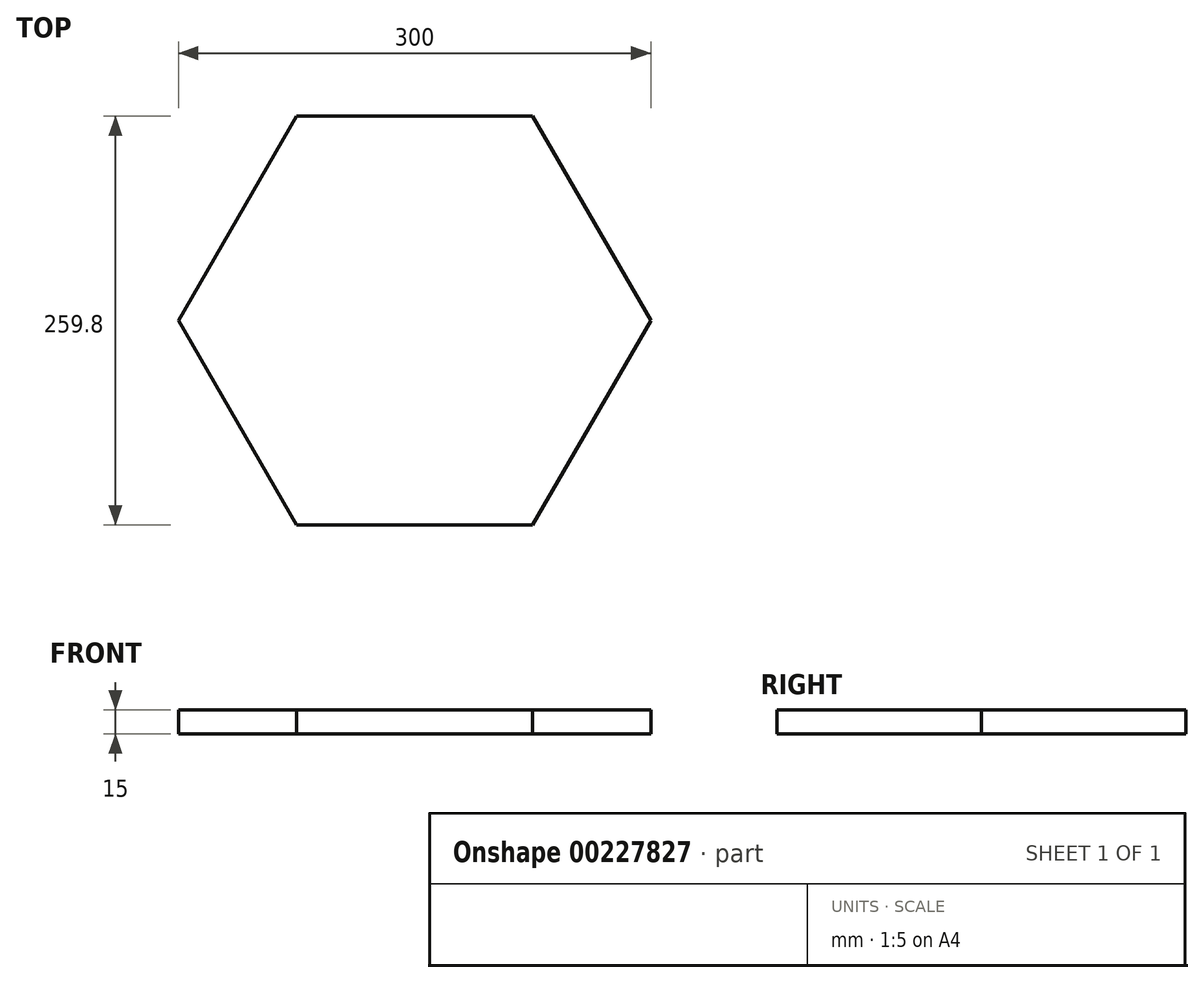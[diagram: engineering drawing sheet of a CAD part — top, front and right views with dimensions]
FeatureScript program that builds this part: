
annotation { "Feature Type Name" : "Feature", "Feature Type Description" : "" }
export const myFeature = defineFeature(function(context is Context, id is Id, definition is map)
    precondition{}
    {
        {
            var Q0;
            Q0=qCreatedBy(makeId("Top.planeOp"),FACE);
            var sketch = newSketch(context, id + "F0", { "sketchPlane" : qUnion([Q0])});
            skCircle(sketch, "E0.cCircle", {"center": v(0, 0) * mm, "radius": 150 * mm, "construction": true});
            skLineSegment(sketch, "E0.0", {"start": v(-150, 0) * mm, "end": v(-75, 129.9) * mm});
            skLineSegment(sketch, "E0.1", {"start": v(-75, 129.9) * mm, "end": v(75, 129.9) * mm});
            skLineSegment(sketch, "E0.2", {"start": v(75, 129.9) * mm, "end": v(150, 0) * mm});
            skLineSegment(sketch, "E0.3", {"start": v(150, 0) * mm, "end": v(75, -129.9) * mm});
            skLineSegment(sketch, "E0.4", {"start": v(75, -129.9) * mm, "end": v(-75, -129.9) * mm});
            skLineSegment(sketch, "E0.5", {"start": v(-75, -129.9) * mm, "end": v(-150, 0) * mm});
            skSolve(sketch);
        }
        {
            var Q0;
            Q0=makeQuery(id+"F0.imprint","IMPRINT",FACE,{"disambiguationData":[TD([[makeQuery(id+"F0.imprint","IMPRINT",EDGE,{"derivedFrom":sQuery(id+"F0.wireOp",EDGE,"E0.0")}),-1.0]])]});
            extrude(context, id + "F1", {"entities" : qUnion([Q0]), "oppositeDirection" : true, "depth" : 15 * mm});
        }
    });
